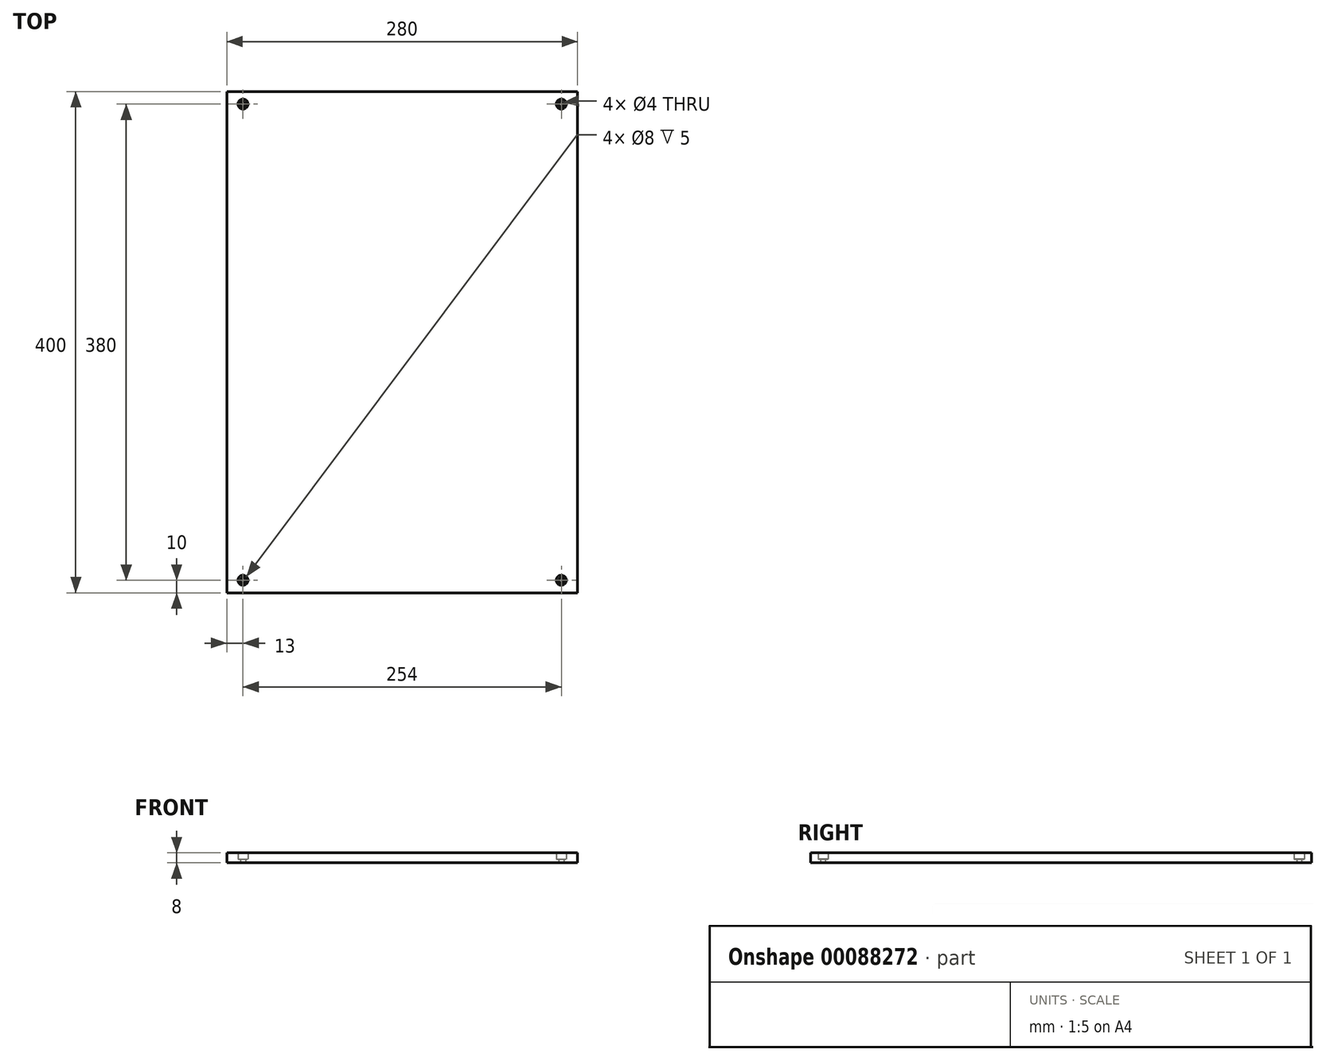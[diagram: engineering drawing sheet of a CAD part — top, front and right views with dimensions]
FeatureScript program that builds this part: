
annotation { "Feature Type Name" : "Feature", "Feature Type Description" : "" }
export const myFeature = defineFeature(function(context is Context, id is Id, definition is map)
    precondition{}
    {
        {
            var Q0;
            Q0=qCreatedBy(makeId("Top.planeOp"),FACE);
            var sketch = newSketch(context, id + "F0", { "sketchPlane" : qUnion([Q0])});
            skLineSegment(sketch, "E0.bottom", {"start": v(140, -200) * mm, "end": v(-140, -200) * mm});
            skLineSegment(sketch, "E0.top", {"start": v(140, 200) * mm, "end": v(-140, 200) * mm});
            skLineSegment(sketch, "E0.left", {"start": v(140, -200) * mm, "end": v(140, 200) * mm});
            skLineSegment(sketch, "E0.right", {"start": v(-140, -200) * mm, "end": v(-140, 200) * mm});
            skPoint(sketch, "E0.middle", {"position": v(0, 0) * mm});
            skSolve(sketch);
        }
        {
            var Q0;
            Q0 = qSketchRegion(id + "F0", true);
            extrude(context, id + "F1", {"entities" : qUnion([Q0]), "depth" : 8 * mm});
        }
        {
            var Q0;
            Q0=makeQuery(id+"F1.opExtrude","CAP_FACE",FACE,{"disambiguationData":[OSD([sQuery(id+"F0.wireOp",EDGE,"E0.bottom"),sQuery(id+"F0.wireOp",EDGE,"E0.top"),sQuery(id+"F0.wireOp",EDGE,"E0.left"),sQuery(id+"F0.wireOp",EDGE,"E0.right")])],"isStart":false});
            var sketch = newSketch(context, id + "F2", { "sketchPlane" : qUnion([Q0])});
            skCircle(sketch, "E1", {"center": v(-127, 190) * mm, "radius": 2 * mm});
            skCircle(sketch, "E2", {"center": v(127, 190) * mm, "radius": 2 * mm});
            skCircle(sketch, "E3", {"center": v(-127, -190) * mm, "radius": 2 * mm});
            skCircle(sketch, "E4", {"center": v(127, -190) * mm, "radius": 2 * mm});
            skSolve(sketch);
        }
        {
            var Q0;
            Q0=sQuery(id+"F2.wireOp",VERTEX,"E1.center");
            var Q1;
            Q1=sQuery(id+"F2.wireOp",VERTEX,"E2.center");
            var Q2;
            Q2=sQuery(id+"F2.wireOp",VERTEX,"E3.center");
            var Q3;
            Q3=sQuery(id+"F2.wireOp",VERTEX,"E4.center");
            var Q4;
            Q4=makeQuery(id+"F1.opExtrude","SWEPT_BODY",BODY,{"disambiguationData":[OSD([sQuery(id+"F0.wireOp",EDGE,"E0.bottom"),sQuery(id+"F0.wireOp",EDGE,"E0.top"),sQuery(id+"F0.wireOp",EDGE,"E0.left"),sQuery(id+"F0.wireOp",EDGE,"E0.right")])]});
            hole(context, id + "F3", {"style" : HoleStyle.C_BORE, "endStyle" : HoleEndStyle.THROUGH, "holeDiameter" : 4 * mm, "cBoreDiameter" : 8 * mm, "cBoreDepth" : 5 * mm, "startFromSketch" : true, "locations" : qUnion([Q0, Q1, Q2, Q3]), "scope" : qUnion([Q4]), "isTappedThrough" : true});
        }
    });
